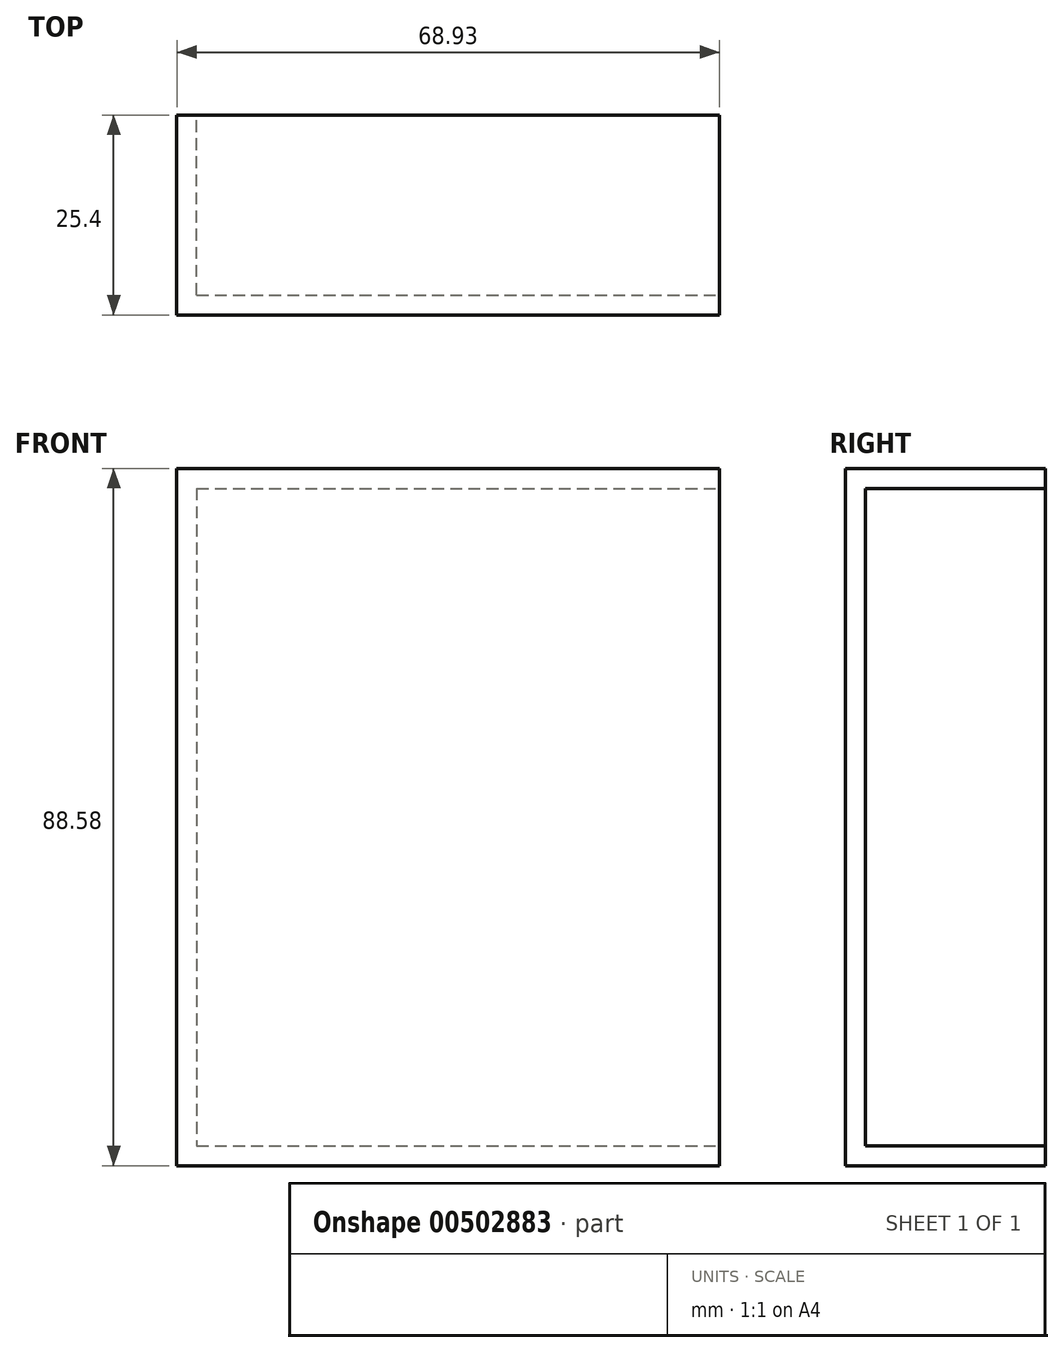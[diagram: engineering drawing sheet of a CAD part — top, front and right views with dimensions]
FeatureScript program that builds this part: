
annotation { "Feature Type Name" : "Feature", "Feature Type Description" : "" }
export const myFeature = defineFeature(function(context is Context, id is Id, definition is map)
    precondition{}
    {
        {
            var Q0;
            Q0=qCreatedBy(makeId("Front.planeOp"),FACE);
            var sketch = newSketch(context, id + "F0", { "sketchPlane" : qUnion([Q0])});
            skLineSegment(sketch, "E0.bottom", {"start": v(-35.87, 58.17) * mm, "end": v(33.06, 58.17) * mm});
            skLineSegment(sketch, "E0.top", {"start": v(-35.87, -30.41) * mm, "end": v(33.06, -30.41) * mm});
            skLineSegment(sketch, "E0.left", {"start": v(-35.87, 58.17) * mm, "end": v(-35.87, -30.41) * mm});
            skLineSegment(sketch, "E0.right", {"start": v(33.06, 58.17) * mm, "end": v(33.06, -30.41) * mm});
            skSolve(sketch);
        }
        {
            var Q0;
            Q0 = qSketchRegion(id + "F0", true);
            extrude(context, id + "F1", {"entities" : qUnion([Q0]), "depth" : 25.4 * mm});
        }
        {
            var Q0;
            Q0=makeQuery(id+"F1.opExtrude","SWEPT_FACE",FACE,{"disambiguationData":[OSD([sQuery(id+"F0.wireOp",EDGE,"E0.right")])]});
            var Q1;
            Q1=makeQuery(id+"F1.opExtrude","CAP_FACE",FACE,{"disambiguationData":[OSD([sQuery(id+"F0.wireOp",EDGE,"E0.bottom"),sQuery(id+"F0.wireOp",EDGE,"E0.top"),sQuery(id+"F0.wireOp",EDGE,"E0.left"),sQuery(id+"F0.wireOp",EDGE,"E0.right")])],"isStart":true});
            shell(context, id + "F2", {"entities" : qUnion([Q0, Q1]), "thickness" : 2.54 * mm});
        }
    });
